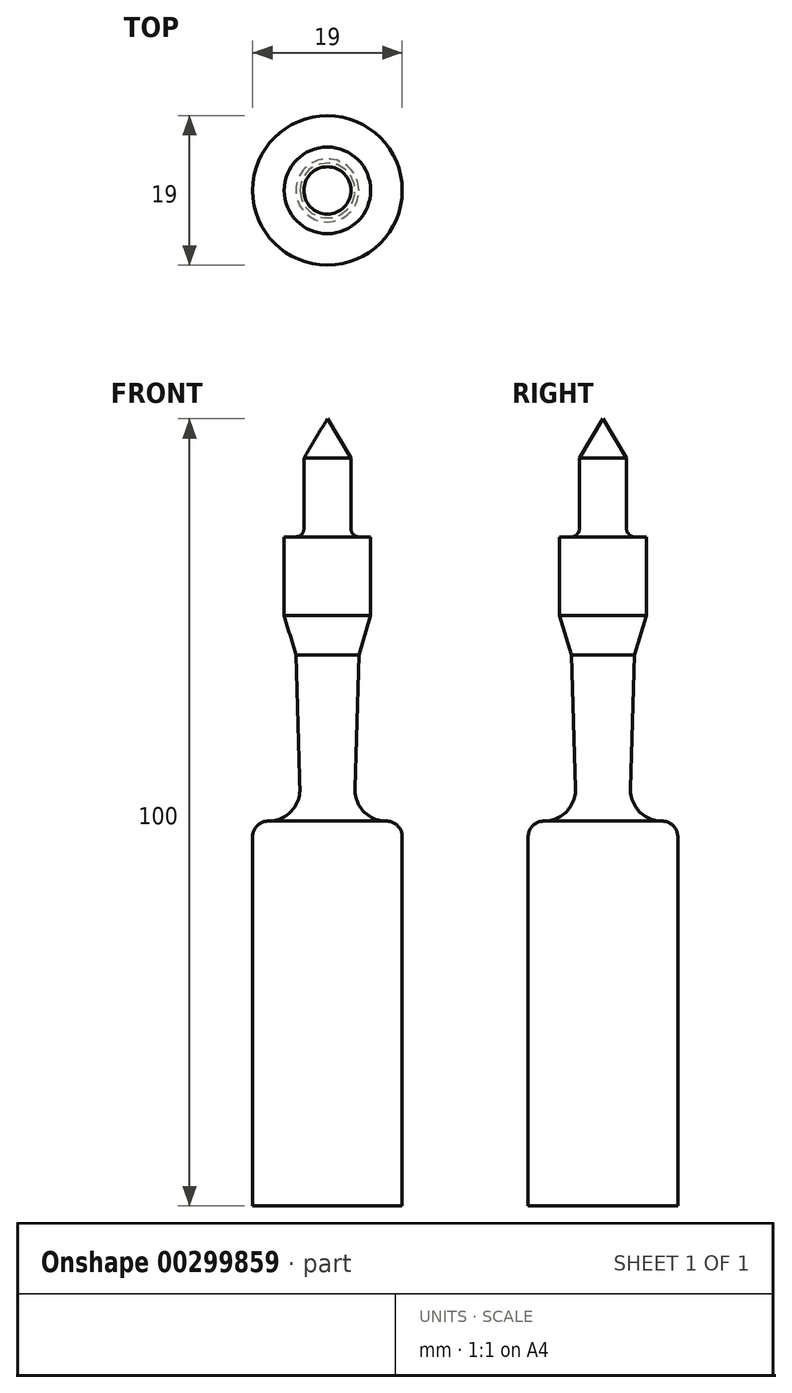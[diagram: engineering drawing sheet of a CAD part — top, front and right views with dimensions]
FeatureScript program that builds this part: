
annotation { "Feature Type Name" : "Feature", "Feature Type Description" : "" }
export const myFeature = defineFeature(function(context is Context, id is Id, definition is map)
    precondition{}
    {
        {
            var Q0;
            Q0=qCreatedBy(makeId("Front.planeOp"),FACE);
            var sketch = newSketch(context, id + "F0", { "sketchPlane" : qUnion([Q0])});
            skLineSegment(sketch, "E0", {"start": v(0, 0) * mm, "end": v(3, -5) * mm});
            skLineSegment(sketch, "E1", {"start": v(3, -5) * mm, "end": v(3, -14) * mm});
            skLineSegment(sketch, "E2", {"start": v(5.5, -25) * mm, "end": v(4, -30) * mm});
            skLineSegment(sketch, "E3", {"start": v(4, -30) * mm, "end": v(3.5, -47) * mm});
            skArc(sketch, "E4", {"start": v(3.5, -47) * mm, "mid": v(4.63, -49.9) * mm, "end": v(7.5, -51.12) * mm});
            skArc(sketch, "E5", {"start": v(9.5, -53.12) * mm, "mid": v(8.91, -51.7) * mm, "end": v(7.5, -51.12) * mm});
            skLineSegment(sketch, "E6", {"start": v(9.5, -53.12) * mm, "end": v(9.5, -100) * mm});
            skLineSegment(sketch, "E7", {"start": v(9.5, -100) * mm, "end": v(0, -100) * mm});
            skLineSegment(sketch, "E8", {"start": v(0, -100) * mm, "end": v(0, 0) * mm});
            skLineSegment(sketch, "E9", {"start": v(5.5, -25) * mm, "end": v(5.5, -15) * mm});
            skLineSegment(sketch, "E10", {"start": v(5.5, -15) * mm, "end": v(4, -15) * mm});
            skArc(sketch, "E11", {"start": v(3, -14) * mm, "mid": v(3.3, -14.7) * mm, "end": v(4, -15) * mm});
            skSolve(sketch);
        }
        {
            var Q0;
            Q0=makeQuery(id+"F0.imprint","IMPRINT",FACE,{"disambiguationData":[TD([[makeQuery(id+"F0.imprint","IMPRINT",EDGE,{"derivedFrom":sQuery(id+"F0.wireOp",EDGE,"E0")}),-1.0]])]});
            var Q1;
            Q1=sQuery(id+"F0.wireOp",EDGE,"E8");
            revolve(context, id + "F1", {"entities" : qUnion([Q0]), "axis" : qUnion([Q1]), "revolveType" : RevolveType.FULL});
        }
    });
